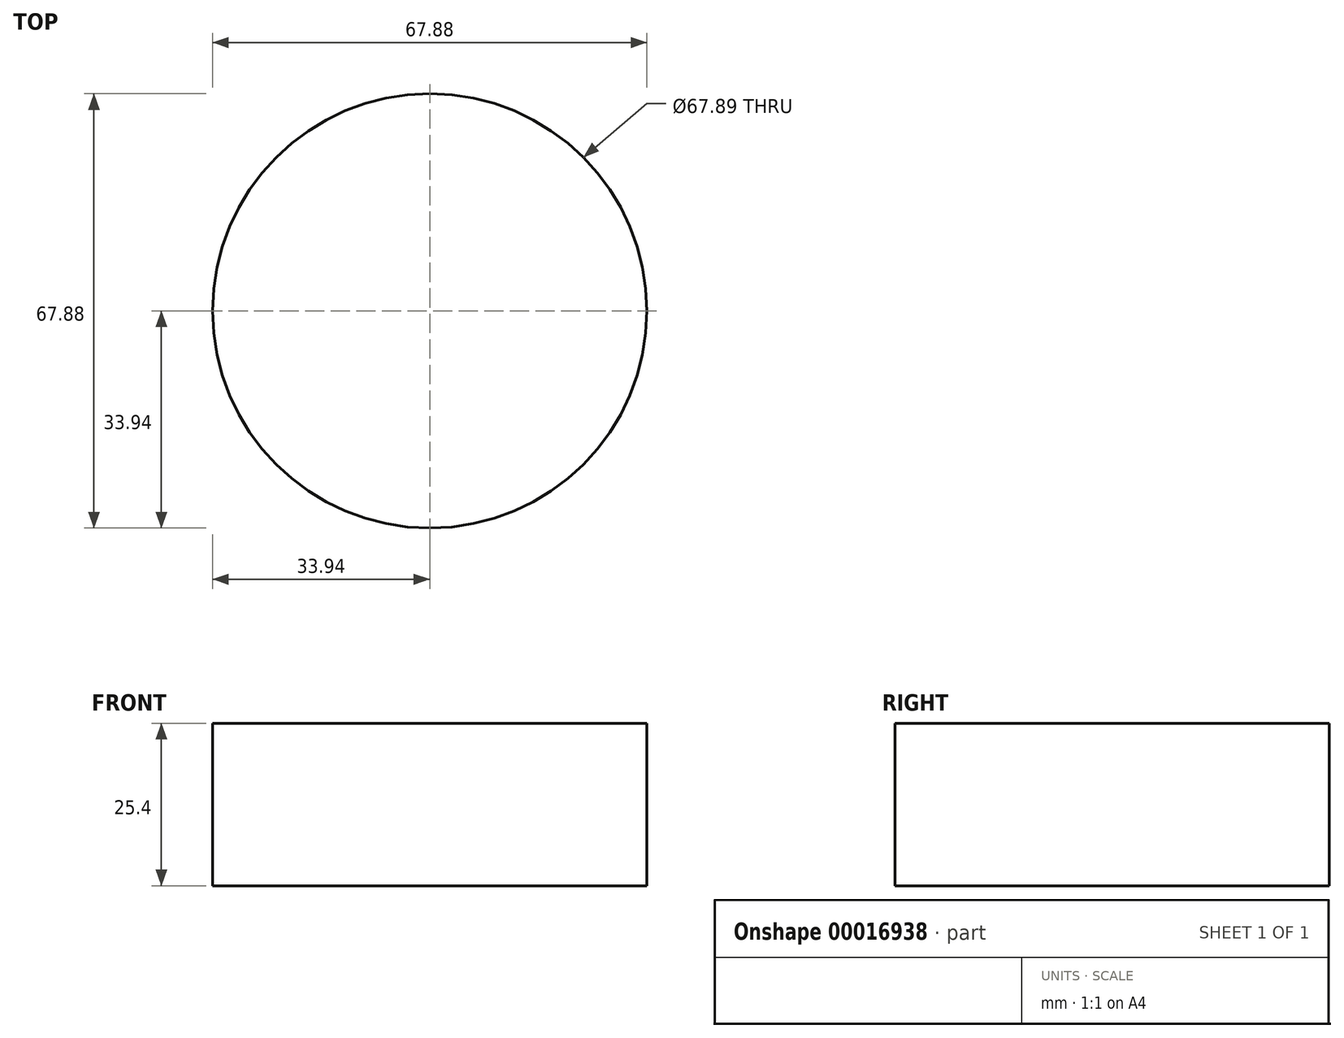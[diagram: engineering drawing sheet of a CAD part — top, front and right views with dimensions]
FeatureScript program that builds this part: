
annotation { "Feature Type Name" : "Feature", "Feature Type Description" : "" }
export const myFeature = defineFeature(function(context is Context, id is Id, definition is map)
    precondition{}
    {
        {
            var Q0;
            Q0=qCreatedBy(makeId("Top.planeOp"),FACE);
            var sketch = newSketch(context, id + "F0", { "sketchPlane" : qUnion([Q0])});
            skCircle(sketch, "E0", {"center": v(0, 0) * mm, "radius": 33.94 * mm});
            skSolve(sketch);
        }
        {
            var Q0;
            Q0=sQuery(id+"F0.wireOp",EDGE,"E0");
            extrude(context, id + "F1", {"bodyType" : ToolBodyType.SURFACE, "surfaceEntities" : qUnion([Q0]), "oppositeDirection" : true, "depth" : 25.4 * mm});
        }
    });
